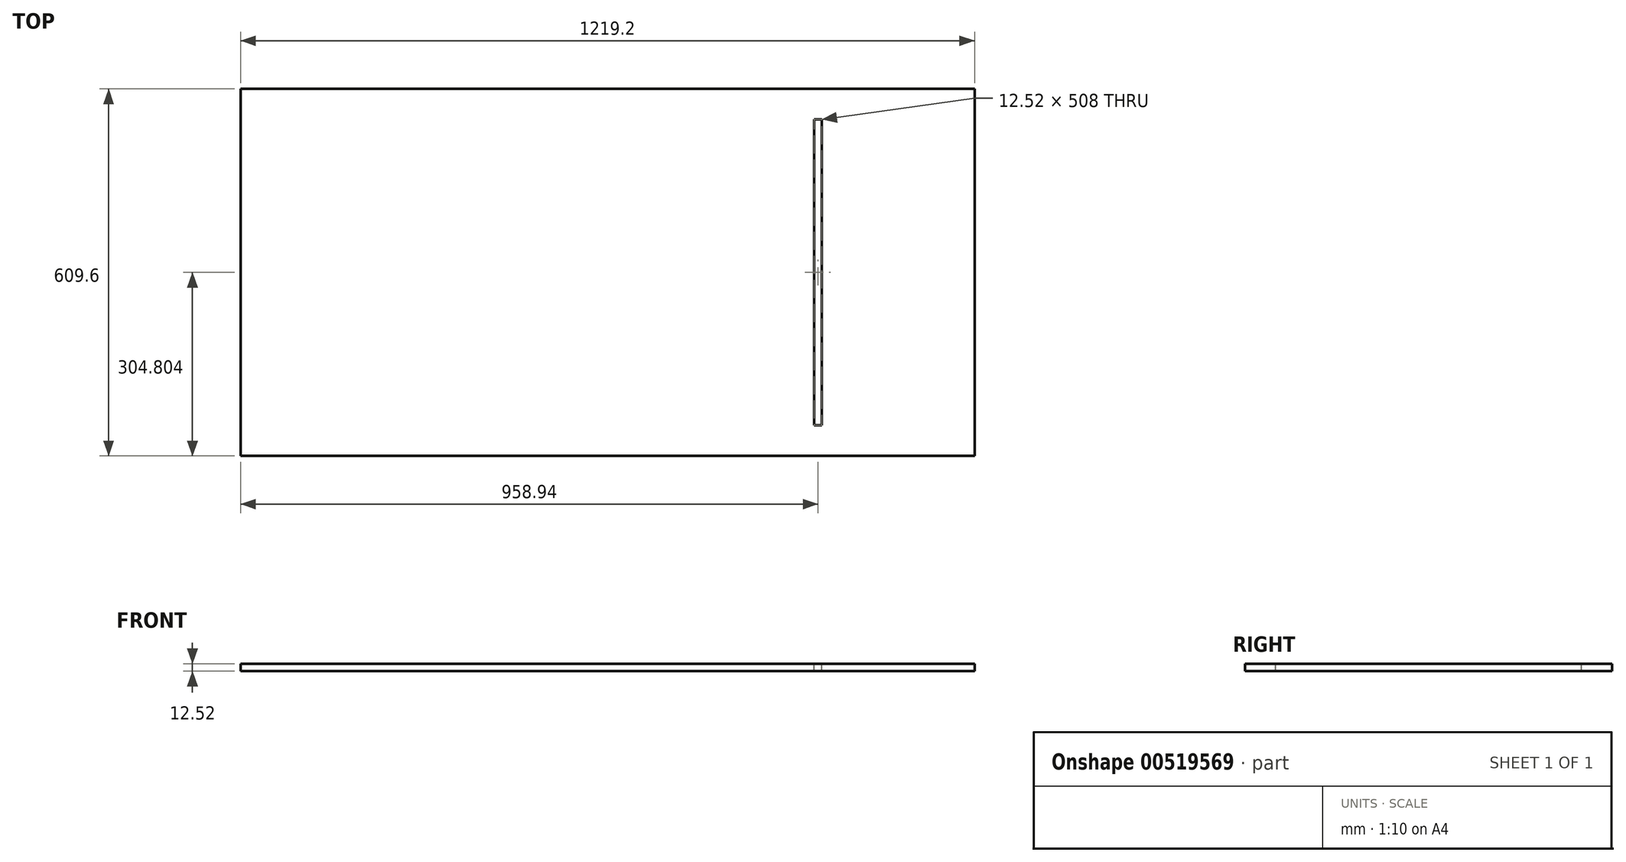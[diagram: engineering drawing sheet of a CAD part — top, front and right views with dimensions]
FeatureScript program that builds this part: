
annotation { "Feature Type Name" : "Feature", "Feature Type Description" : "" }
export const myFeature = defineFeature(function(context is Context, id is Id, definition is map)
    precondition{}
    {
        {
            var Q0;
            Q0=qCreatedBy(makeId("Top.planeOp"),FACE);
            var sketch = newSketch(context, id + "F0", { "sketchPlane" : qUnion([Q0])});
            skLineSegment(sketch, "E0.bottom", {"start": v(-63.39, 570) * mm, "end": v(1155.81, 570) * mm});
            skLineSegment(sketch, "E0.top", {"start": v(-63.39, -39.6) * mm, "end": v(1155.81, -39.6) * mm});
            skLineSegment(sketch, "E0.left", {"start": v(-63.39, 570) * mm, "end": v(-63.39, -39.6) * mm});
            skLineSegment(sketch, "E0.right", {"start": v(1155.81, 570) * mm, "end": v(1155.81, -39.6) * mm});
            skSolve(sketch);
        }
        {
            var Q0;
            Q0 = qSketchRegion(id + "F0", true);
            extrude(context, id + "F1", {"entities" : qUnion([Q0]), "depth" : 12.52 * mm, "offsetDistance" : 25.4 * mm});
        }
        {
            var Q0;
            Q0=makeQuery(id+"F1.opExtrude","CAP_FACE",FACE,{"disambiguationData":[OSD([sQuery(id+"F0.wireOp",EDGE,"E0.bottom"),sQuery(id+"F0.wireOp",EDGE,"E0.top"),sQuery(id+"F0.wireOp",EDGE,"E0.left"),sQuery(id+"F0.wireOp",EDGE,"E0.right")])],"isStart":false});
            var sketch = newSketch(context, id + "F2", { "sketchPlane" : qUnion([Q0])});
            skLineSegment(sketch, "E1.bottom", {"start": v(889.29, 519.2) * mm, "end": v(901.81, 519.2) * mm});
            skLineSegment(sketch, "E1.top", {"start": v(889.29, 11.2) * mm, "end": v(901.81, 11.2) * mm});
            skLineSegment(sketch, "E1.left", {"start": v(889.29, 519.2) * mm, "end": v(889.29, 11.2) * mm});
            skLineSegment(sketch, "E1.right", {"start": v(901.81, 519.2) * mm, "end": v(901.81, 11.2) * mm});
            skSolve(sketch);
        }
        {
            var Q0;
            Q0=makeQuery(id+"F2.imprint","IMPRINT",FACE,{"disambiguationData":[TD([[makeQuery(id+"F2.imprint","IMPRINT",EDGE,{"derivedFrom":sQuery(id+"F2.wireOp",EDGE,"E1.bottom")}),-1.0]])]});
            extrude(context, id + "F3", {"entities" : qUnion([Q0]), "operationType" : NewBodyOperationType.REMOVE, "endBound" : BoundingType.THROUGH_ALL, "oppositeDirection" : true, "depth" : 25.4 * mm, "offsetDistance" : 25.4 * mm});
        }
    });
